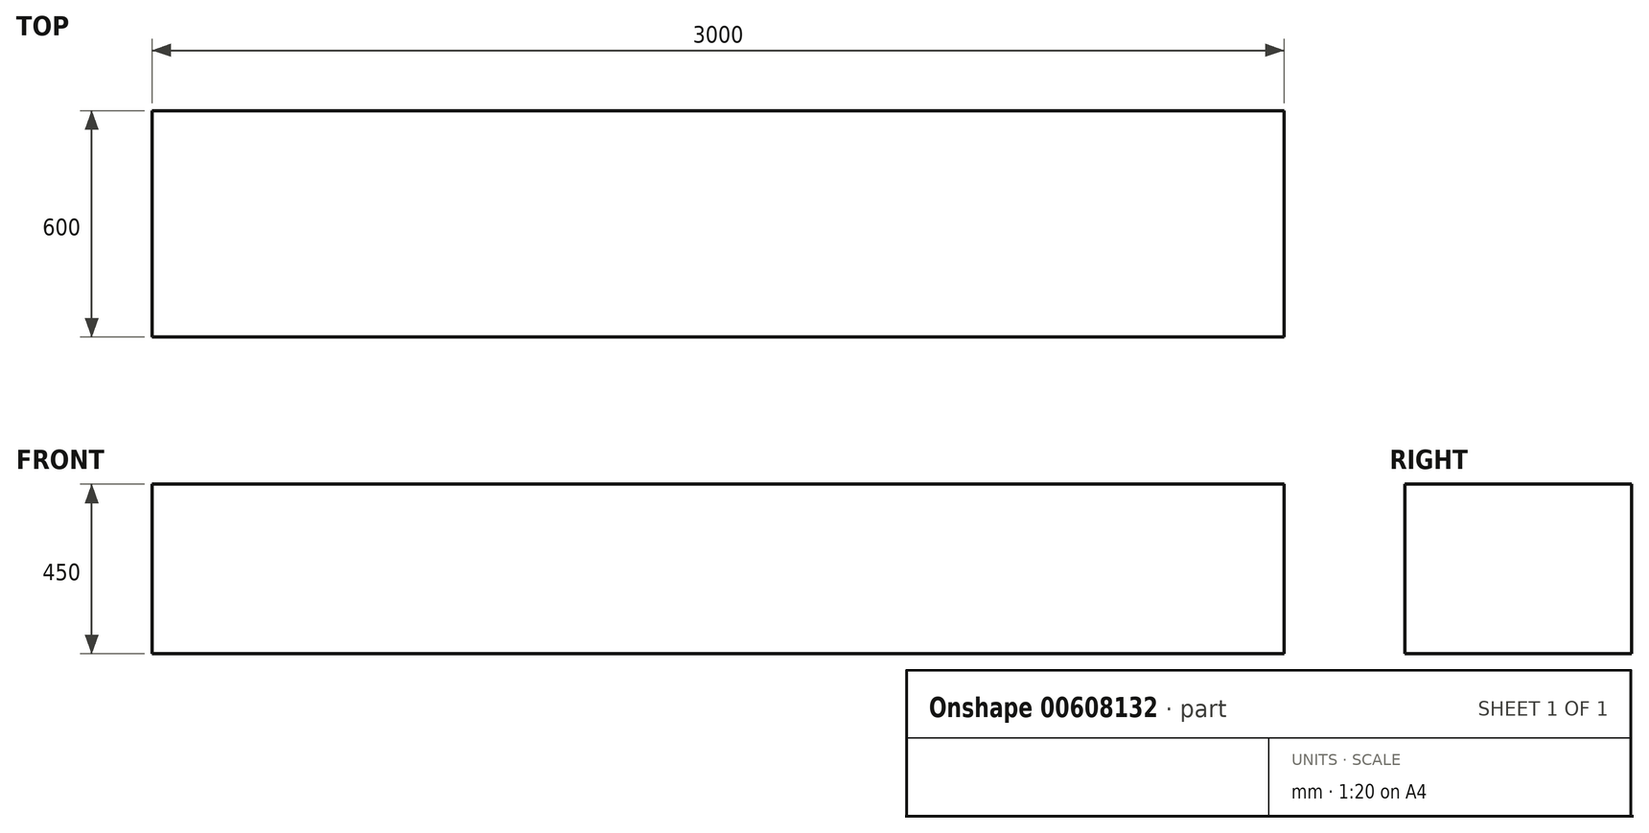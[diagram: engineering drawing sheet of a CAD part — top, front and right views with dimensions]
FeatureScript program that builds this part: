
annotation { "Feature Type Name" : "Feature", "Feature Type Description" : "" }
export const myFeature = defineFeature(function(context is Context, id is Id, definition is map)
    precondition{}
    {
        {
            var Q0;
            Q0=qCreatedBy(makeId("Front.planeOp"),FACE);
            var sketch = newSketch(context, id + "F0", { "sketchPlane" : qUnion([Q0])});
            skLineSegment(sketch, "E0.bottom", {"start": v(3000, 450) * mm, "end": v(0, 450) * mm});
            skLineSegment(sketch, "E0.top", {"start": v(3000, 0) * mm, "end": v(0, 0) * mm});
            skLineSegment(sketch, "E0.left", {"start": v(3000, 450) * mm, "end": v(3000, 0) * mm});
            skLineSegment(sketch, "E0.right", {"start": v(0, 450) * mm, "end": v(0, 0) * mm});
            skSolve(sketch);
        }
        {
            var Q0;
            Q0=makeQuery(id+"F0.imprint","IMPRINT",FACE,{"disambiguationData":[TD([[makeQuery(id+"F0.imprint","IMPRINT",EDGE,{"derivedFrom":sQuery(id+"F0.wireOp",EDGE,"E0.bottom")}),1.0]])]});
            var sketch = newSketch(context, id + "F1", { "sketchPlane" : qUnion([Q0])});
            skSolve(sketch);
        }
        {
            var Q0;
            Q0=makeQuery(id+"F1.imprint","IMPRINT",FACE,{"disambiguationData":[TD([[makeQuery(id+"F1.imprint","IMPRINT",EDGE,{"derivedFrom":makeQuery(id+"F0.imprint","IMPRINT",EDGE,{"derivedFrom":sQuery(id+"F0.wireOp",EDGE,"E0.bottom")})}),1.0]])]});
            extrude(context, id + "F2", {"entities" : qUnion([Q0]), "depth" : 600 * mm, "offsetDistance" : 25 * mm});
        }
    });
